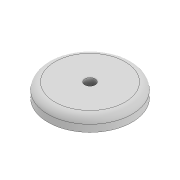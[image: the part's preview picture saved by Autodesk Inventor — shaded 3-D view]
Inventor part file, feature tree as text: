
AUTODESK INVENTOR PART (.ipt)
format: ipt  version: 2022 (Build 260153000, 153)  size: 102,912 bytes
history: native  units: mm
features: extrude x1, fillet x1, sketch x1
ambient origin geometry x8: Origin, YZ Plane, XZ Plane, XY Plane, X Axis, Y Axis, Z Axis, Center Point
bodies: Solid1 (feature_tree)
feature tree (3):
  extrude  "Extrusion1"  Depth=1.0mm
  fillet  "Fillet1"  Radius=2.0mm
  sketch  "Sketch1"  dims[d0=1.5mm d1=12.0mm d2=2.0mm d3=0.0mm d4=1.0mm]
